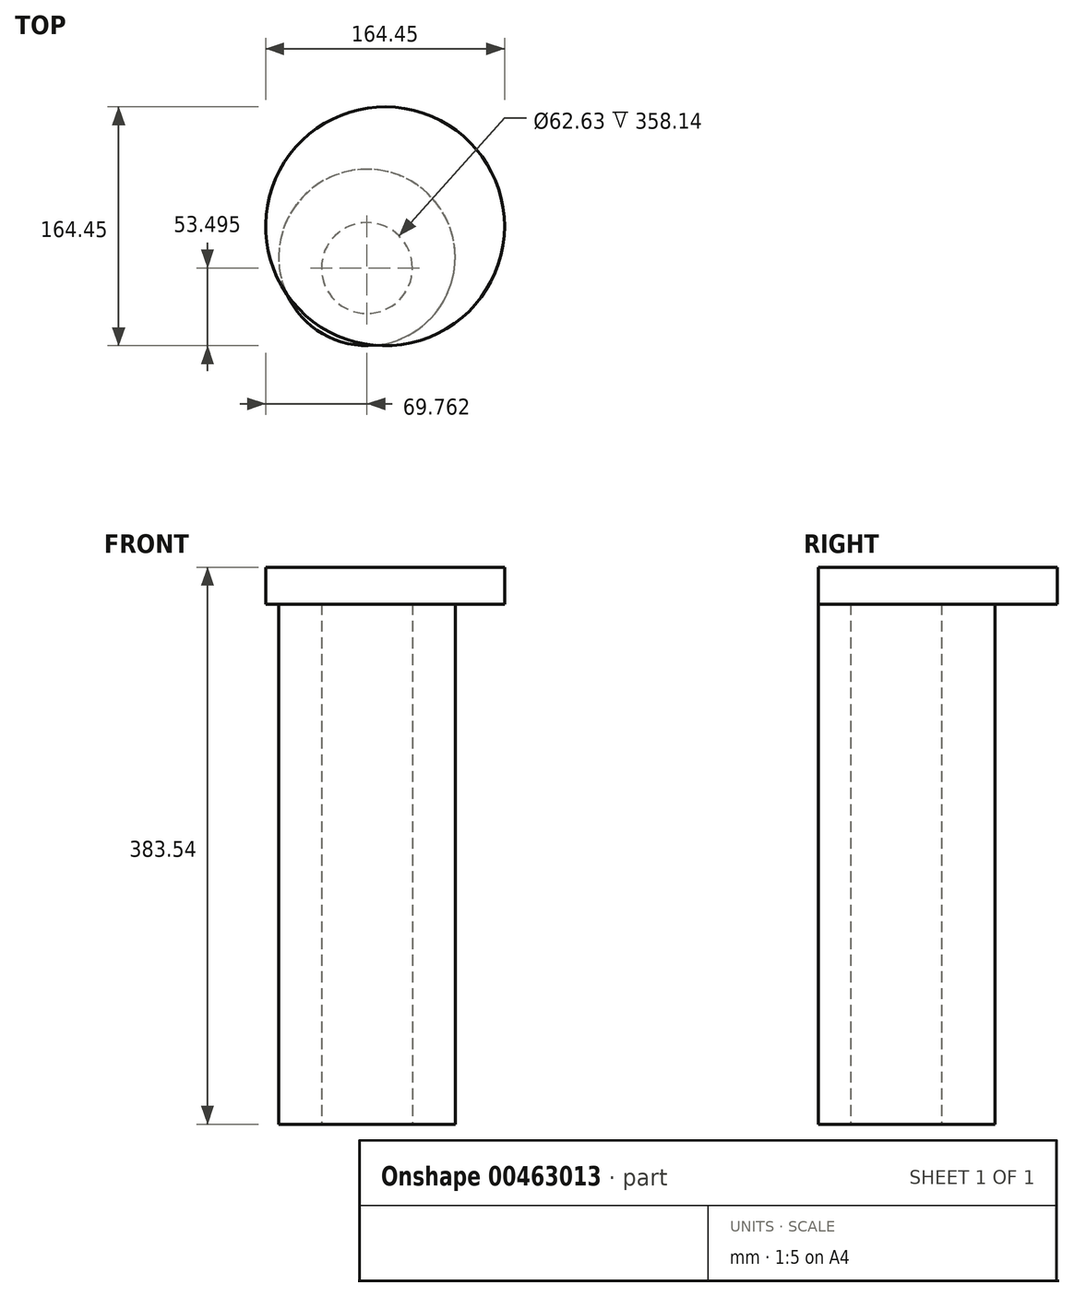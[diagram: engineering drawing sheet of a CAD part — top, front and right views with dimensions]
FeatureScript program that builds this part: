
annotation { "Feature Type Name" : "Feature", "Feature Type Description" : "" }
export const myFeature = defineFeature(function(context is Context, id is Id, definition is map)
    precondition{}
    {
        {
            var Q0;
            Q0=qCreatedBy(makeId("Top.planeOp"),FACE);
            var sketch = newSketch(context, id + "F0", { "sketchPlane" : qUnion([Q0])});
            skCircle(sketch, "E0", {"center": v(-35.67, -22.93) * mm, "radius": 31.32 * mm});
            skCircle(sketch, "E1", {"center": v(-35.67, -22.93) * mm, "radius": 21.07 * mm});
            skCircle(sketch, "E2", {"center": v(-35.67, -15.67) * mm, "radius": 60.74 * mm});
            skSolve(sketch);
        }
        {
            var Q0;
            Q0 = qSketchRegion(id + "F0", true);
            extrude(context, id + "F1", {"entities" : qUnion([Q0]), "depth" : 358.14 * mm});
        }
        {
            var Q0;
            Q0=makeQuery(id+"F1.opExtrude","CAP_FACE",FACE,{"disambiguationData":[OSD([sQuery(id+"F0.wireOp",EDGE,"E0"),sQuery(id+"F0.wireOp",EDGE,"E2")])],"isStart":false});
            var sketch = newSketch(context, id + "F2", { "sketchPlane" : qUnion([Q0])});
            skCircle(sketch, "E3", {"center": v(-23.2, 5.8) * mm, "radius": 82.22 * mm});
            skSolve(sketch);
        }
        {
            var Q0;
            Q0 = qSketchRegion(id + "F2", true);
            extrude(context, id + "F3", {"entities" : qUnion([Q0]), "operationType" : NewBodyOperationType.ADD, "depth" : 25.4 * mm});
        }
    });
